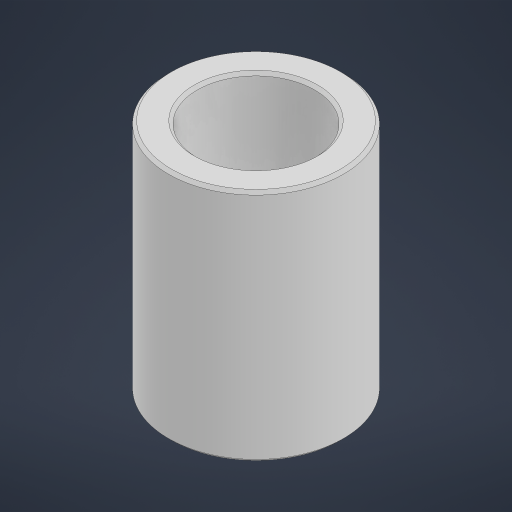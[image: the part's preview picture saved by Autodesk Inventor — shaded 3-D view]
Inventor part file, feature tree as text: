
AUTODESK INVENTOR PART (.ipt)
format: ipt  version: 2023 (Build 270158000, 158)  size: 174,080 bytes
history: native  units: in
note: dims shown in document units (in); Inventor stores cm internally (conversion verified against a paired STEP export)
features: chamfer x1
ambient origin geometry x8: Origin, YZ Plane, XZ Plane, XY Plane, X Axis, Y Axis, Z Axis, Center Point
bodies: Solid1 (feature_tree)
feature tree (1):
  chamfer  "Chamfer1"  [1 undecoded]
note: 1 required parameter value undecoded (feature->parameter linkage not recoverable at this tier; creation-order binding heuristic only, values carry confidence <= 0.55)
